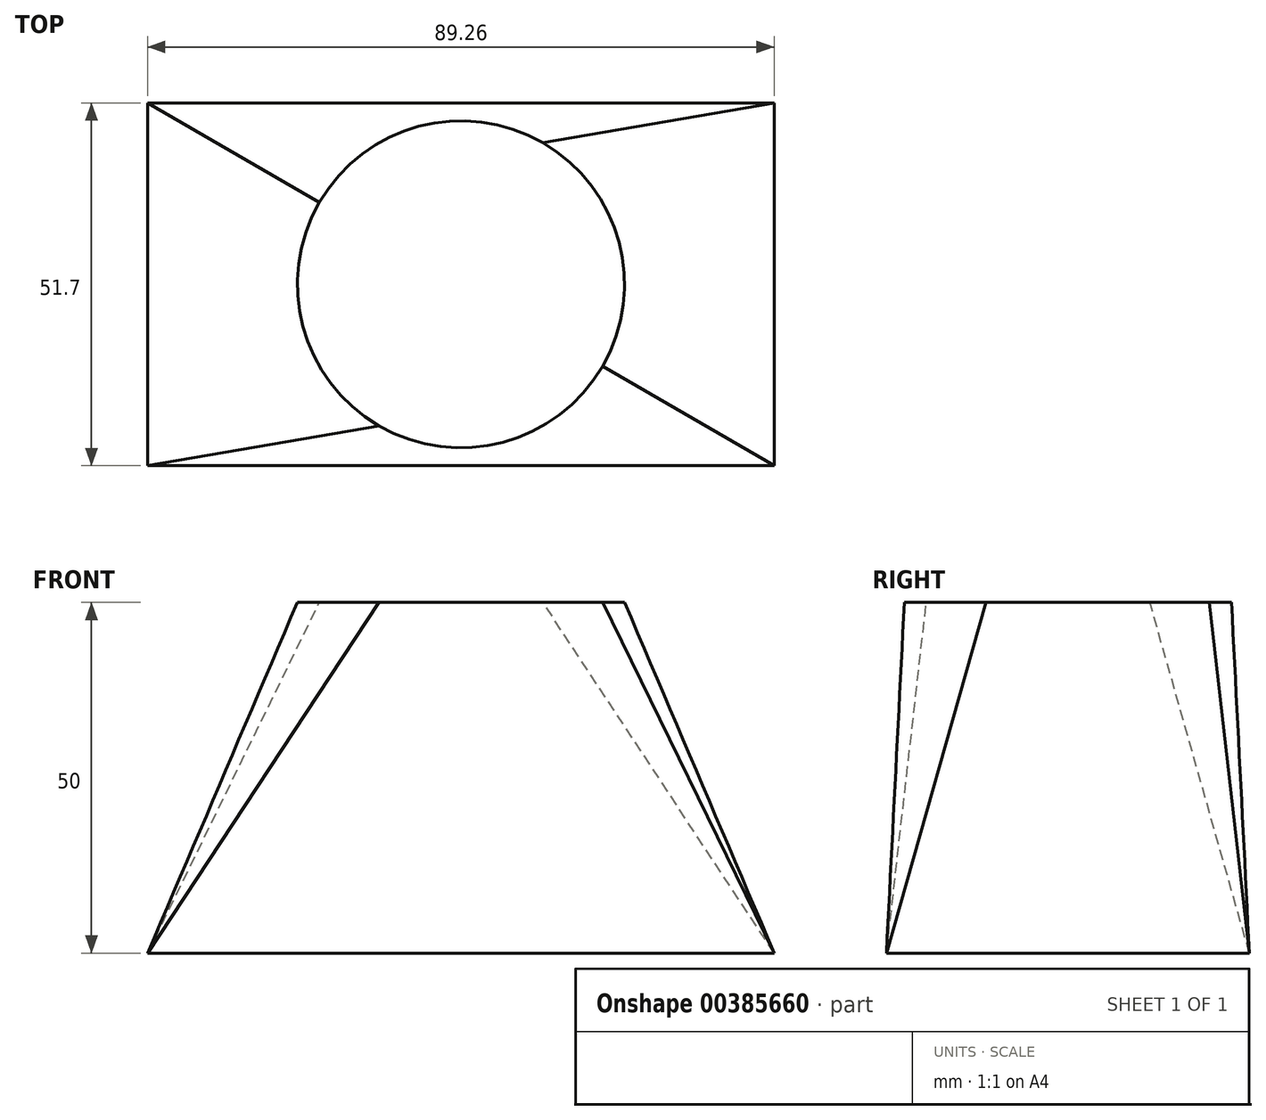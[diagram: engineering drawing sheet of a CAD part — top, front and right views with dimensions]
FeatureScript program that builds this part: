
annotation { "Feature Type Name" : "Feature", "Feature Type Description" : "" }
export const myFeature = defineFeature(function(context is Context, id is Id, definition is map)
    precondition{}
    {
        {
            var Q0;
            Q0=qCreatedBy(makeId("Top.planeOp"),FACE);
            var sketch = newSketch(context, id + "F0", { "sketchPlane" : qUnion([Q0])});
            skLineSegment(sketch, "E0.bottom", {"start": v(44.63, -25.85) * mm, "end": v(-44.63, -25.85) * mm});
            skLineSegment(sketch, "E0.top", {"start": v(44.63, 25.85) * mm, "end": v(-44.63, 25.85) * mm});
            skLineSegment(sketch, "E0.left", {"start": v(44.63, -25.85) * mm, "end": v(44.63, 25.85) * mm});
            skLineSegment(sketch, "E0.right", {"start": v(-44.63, -25.85) * mm, "end": v(-44.63, 25.85) * mm});
            skPoint(sketch, "E0.middle", {"position": v(0, 0) * mm});
            skSolve(sketch);
        }
        {
            var Q0;
            Q0=qCreatedBy(makeId("Top.planeOp"),FACE);
            cPlane(context, id + "F1", {"entities" : qUnion([Q0]), "cplaneType" : CPlaneType.OFFSET, "offset" : 50 * mm, "width" : 150 * mm, "height" : 150 * mm});
        }
        {
            var Q0;
            Q0=qCreatedBy(id+"F1.planeOp",FACE);
            var sketch = newSketch(context, id + "F2", { "sketchPlane" : qUnion([Q0])});
            skCircle(sketch, "E1", {"center": v(0, 0) * mm, "radius": 23.3 * mm});
            skSolve(sketch);
        }
        {
            var Q0;
            Q0=qCreatedBy(id+"F1.planeOp",FACE);
            cPlane(context, id + "F3", {"entities" : qUnion([Q0]), "cplaneType" : CPlaneType.OFFSET, "offset" : 25 * mm, "width" : 150 * mm, "height" : 150 * mm});
        }
        {
            var Q0;
            Q0=makeQuery(id+"F0.imprint","IMPRINT",FACE,{"disambiguationData":[TD([[makeQuery(id+"F0.imprint","IMPRINT",EDGE,{"derivedFrom":sQuery(id+"F0.wireOp",EDGE,"E0.bottom")}),-1.0]])]});
            var Q1;
            Q1=makeQuery(id+"F2.imprint","IMPRINT",FACE,{"disambiguationData":[TD([[makeQuery(id+"F2.imprint","IMPRINT",EDGE,{"derivedFrom":sQuery(id+"F2.wireOp",EDGE,"E1")}),1.0]])]});
            loft(context, id + "F4", {"sheetProfilesArray" : [{ "sheetProfileEntities" : qUnion([Q0]) }, { "sheetProfileEntities" : qUnion([Q1]) }]});
        }
    });
